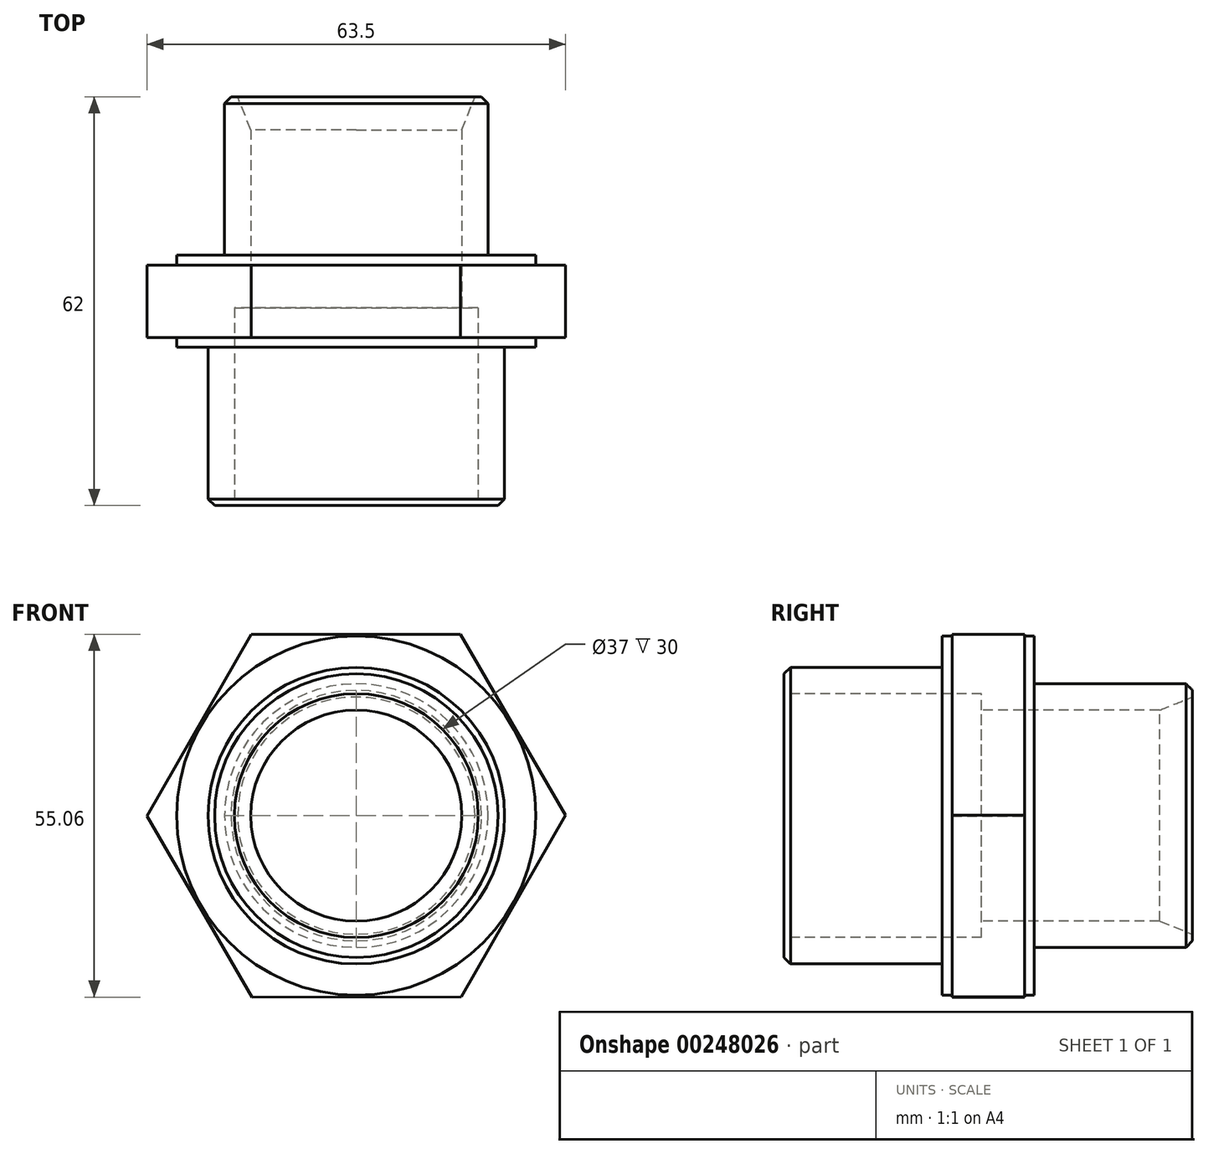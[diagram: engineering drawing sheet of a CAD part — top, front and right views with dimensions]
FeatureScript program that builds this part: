
annotation { "Feature Type Name" : "Feature", "Feature Type Description" : "" }
export const myFeature = defineFeature(function(context is Context, id is Id, definition is map)
    precondition{}
    {
        {
            var Q0;
            Q0=qCreatedBy(makeId("Front.planeOp"),FACE);
            var sketch = newSketch(context, id + "F0", { "sketchPlane" : qUnion([Q0])});
            skLineSegment(sketch, "E0.0", {"start": v(15.83, 27.53) * mm, "end": v(31.75, 0.05) * mm});
            skLineSegment(sketch, "E0.1", {"start": v(31.75, 0.05) * mm, "end": v(15.92, -27.47) * mm});
            skLineSegment(sketch, "E0.2", {"start": v(15.92, -27.47) * mm, "end": v(-15.83, -27.53) * mm});
            skLineSegment(sketch, "E0.3", {"start": v(-15.83, -27.53) * mm, "end": v(-31.75, -0.05) * mm});
            skLineSegment(sketch, "E0.4", {"start": v(-31.75, -0.05) * mm, "end": v(-15.92, 27.47) * mm});
            skLineSegment(sketch, "E0.5", {"start": v(-15.92, 27.47) * mm, "end": v(15.83, 27.53) * mm});
            skPoint(sketch, "E0.0.midPoint", {"position": v(23.8, 13.79) * mm});
            skSolve(sketch);
        }
        {
            var Q0;
            Q0 = qSketchRegion(id + "F0", true);
            extrude(context, id + "F1", {"entities" : qUnion([Q0]), "depth" : 11 * mm, "offsetDistance" : 25 * mm, "symmetric" : true});
        }
        {
            var Q0;
            Q0=qCreatedBy(makeId("Front.planeOp"),FACE);
            var sketch = newSketch(context, id + "F2", { "sketchPlane" : qUnion([Q0])});
            skCircle(sketch, "E1", {"center": v(0, 0) * mm, "radius": 27.25 * mm});
            skSolve(sketch);
        }
        {
            var Q0;
            Q0 = qSketchRegion(id + "F2", true);
            extrude(context, id + "F3", {"entities" : qUnion([Q0]), "operationType" : NewBodyOperationType.ADD, "depth" : 14 * mm, "offsetDistance" : 25 * mm, "symmetric" : true});
        }
        {
            var Q0;
            Q0=makeQuery(id+"F3.opExtrude","CAP_FACE",FACE,{"disambiguationData":[OSD([sQuery(id+"F2.wireOp",EDGE,"E1")])],"isStart":false});
            var sketch = newSketch(context, id + "F4", { "sketchPlane" : qUnion([Q0])});
            skCircle(sketch, "E2", {"center": v(0, 0) * mm, "radius": 22.5 * mm});
            skSolve(sketch);
        }
        {
            var Q0;
            Q0 = qSketchRegion(id + "F4", true);
            var Q1;
            Q1=makeQuery(id+"F4.imprint","IMPRINT",FACE,{"disambiguationData":[TD([[makeQuery(id+"F4.imprint","IMPRINT",EDGE,{"derivedFrom":sQuery(id+"F4.wireOp",EDGE,"E2")}),1.0]])]});
            extrude(context, id + "F5", {"entities" : qUnion([Q0, Q1]), "operationType" : NewBodyOperationType.ADD, "depth" : 24 * mm, "offsetDistance" : 25 * mm});
        }
        {
            var Q0;
            Q0=makeQuery(id+"F3.opExtrude","CAP_FACE",FACE,{"disambiguationData":[OSD([sQuery(id+"F2.wireOp",EDGE,"E1")])],"isStart":true});
            var sketch = newSketch(context, id + "F6", { "sketchPlane" : qUnion([Q0])});
            skCircle(sketch, "E3", {"center": v(0, 0) * mm, "radius": 20 * mm});
            skSolve(sketch);
        }
        {
            var Q0;
            Q0=makeQuery(id+"F6.imprint","IMPRINT",FACE,{"disambiguationData":[TD([[makeQuery(id+"F6.imprint","IMPRINT",EDGE,{"derivedFrom":sQuery(id+"F6.wireOp",EDGE,"E3")}),1.0]])]});
            extrude(context, id + "F7", {"entities" : qUnion([Q0]), "operationType" : NewBodyOperationType.ADD, "depth" : 24 * mm, "offsetDistance" : 25 * mm});
        }
        {
            var Q0;
            Q0=makeQuery(id+"F5.opExtrude","CAP_FACE",FACE,{"disambiguationData":[OSD([sQuery(id+"F4.wireOp",EDGE,"E2")])],"isStart":false});
            var sketch = newSketch(context, id + "F8", { "sketchPlane" : qUnion([Q0])});
            skCircle(sketch, "E4", {"center": v(0, 0) * mm, "radius": 16 * mm});
            skSolve(sketch);
        }
        {
            var Q0;
            Q0=makeQuery(id+"F8.imprint","IMPRINT",FACE,{"disambiguationData":[TD([[makeQuery(id+"F8.imprint","IMPRINT",EDGE,{"derivedFrom":sQuery(id+"F8.wireOp",EDGE,"E4")}),1.0]])]});
            extrude(context, id + "F9", {"entities" : qUnion([Q0]), "operationType" : NewBodyOperationType.REMOVE, "endBound" : BoundingType.THROUGH_ALL, "oppositeDirection" : true, "depth" : 25 * mm, "offsetDistance" : 25 * mm});
        }
        {
            var Q0;
            Q0=makeQuery(id+"F5.opExtrude","CAP_FACE",FACE,{"disambiguationData":[OSD([sQuery(id+"F4.wireOp",EDGE,"E2")])],"isStart":false});
            var sketch = newSketch(context, id + "F10", { "sketchPlane" : qUnion([Q0])});
            skCircle(sketch, "E5", {"center": v(0, 0) * mm, "radius": 18.5 * mm});
            skSolve(sketch);
        }
        {
            var Q0;
            Q0 = qSketchRegion(id + "F10", true);
            extrude(context, id + "F11", {"entities" : qUnion([Q0]), "operationType" : NewBodyOperationType.REMOVE, "oppositeDirection" : true, "depth" : 30 * mm, "offsetDistance" : 25 * mm});
        }
        {
            var Q0;
            Q0=makeQuery(id+"F5.opExtrude","CAP_EDGE",EDGE,{"disambiguationData":[OSD([sQuery(id+"F4.wireOp",EDGE,"E2")])],"isStart":false});
            var Q1;
            Q1=makeQuery(id+"F7.opExtrude","CAP_EDGE",EDGE,{"disambiguationData":[OSD([sQuery(id+"F6.wireOp",EDGE,"E3")])],"isStart":false});
            chamfer(context, id + "F12", {"entities" : qUnion([Q0, Q1]), "width" : 1 * mm, "tangentPropagation" : true});
        }
        {
            var Q0;
            Q0=makeQuery(id+"F9.boolean.opBoolean","INTERSECT",EDGE,{"derivedFrom":[makeQuery(id+"F7.opExtrude","CAP_FACE",FACE,{"disambiguationData":[OSD([sQuery(id+"F6.wireOp",EDGE,"E3")])],"isStart":false}),makeQuery(id+"F9.opExtrude","SWEPT_FACE",FACE,{"disambiguationData":[OSD([sQuery(id+"F8.wireOp",EDGE,"E4")])]})]});
            var Q1;
            Q1=makeQuery(id+"F11.boolean.opBoolean","COPY",EDGE,{"derivedFrom":makeQuery(id+"F11.opExtrude","CAP_EDGE",EDGE,{"disambiguationData":[OSD([sQuery(id+"F10.wireOp",EDGE,"E5")])],"isStart":true})});
            chamfer(context, id + "F13", {"entities" : qUnion([Q0, Q1]), "chamferType" : ChamferType.TWO_OFFSETS, "width1" : 5 * mm, "oppositeDirection" : false, "width2" : 2 * mm, "tangentPropagation" : true});
        }
    });
